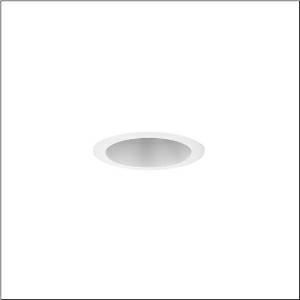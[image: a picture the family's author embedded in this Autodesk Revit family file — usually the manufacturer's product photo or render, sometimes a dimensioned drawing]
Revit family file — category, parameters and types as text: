
# Revit family: lunis_31_mini_51dn16de31
name_source: partatom
category: Lighting Fixtures
units: mm (PartAtom-declared; Revit-internal decimal feet)

## family parameters
Cut with Voids When Loaded = No
Host = Face
Light Source = No
Part Type = Normal
Room Calculation Point = No
Round Connector Dimension = Use Diameter
Shared = No

## types (1)
- Lunis 31 mini (1 x LED, 1000 lm, 8.3 W, 3000K)
    Apparent Load = 8 VA
    CIE Flux Codes = 69 93 99 100 100
    Color Rendering = 80
    Color Temperature = 3000K
    Default Elevation = 1800 mm
    Description = Lunis 31,  mini, downlight, light control with reflector, light emission: direct distribution, LED rated luminous flux: 1.000lm, light colour: 830, mains connection: 220..240V, AC, 50/60Hz, housing, white, protection rating (complete): IP20, protection rating (on room side): IP54, insulation class (complete): insulation class II (safety insulation), certification: CE, packaging unit: 1 piece
    Height = 0 mm  [stored 0 ft]
    Lamp = 1 x LED
    Lamp Light Flux = 1000 lm
    Lamp Power = 8.3 W
    Lamp count = 1
    Length = 188 mm  [stored 0.616798 ft]
    Luminous efficacy = 120 lm/W
    Manufacturer = Siteco
    ModVariant = No
    Model = 51DN16DE31
    Mounting Place = Ceiling
    Mounting Type = Recessed
    Number of Poles = 1
    OnlyDefault = Yes
    Power Factor = 1
    Product Name = Lunis 31 mini
    Product group = downlight
    ProductGroupID = 400
    Protection Class = Protection class II
    Protection Degree = IP 20
    RLX_Detail_Level = 1
    RLX_Emergency_Light_Flux = 0 lm
    RLX_Emergency_Type = 0
    RLX_Emergency_Type_DB = No
    RlxData = <blob elided: 21869 chars, md5=fcc25515>
    Socket = socket
    Standby Power = 0 W
    System Light Flux = 1000 lm
    System Power = 8 W
    Type Comments = Product without accessories
    Type Image = l_1345911.jpg
    URL = http://relux.com
    VarID = ---
    Voltage = 0 V
    Weight = 0.00 kg
    Width = 0 mm  [stored 0 ft]

note: [stored X ft] marks values corroborated as IEEE doubles in the binary element streams (Revit-internal decimal feet)

## geometry (parser evidence)
native form markers: Blend x4, Sweep x12
no freeform markers — native parametric forms only
